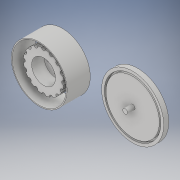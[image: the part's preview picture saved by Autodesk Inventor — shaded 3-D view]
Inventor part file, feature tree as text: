
AUTODESK INVENTOR PART (.ipt)
format: ipt  version: 2017 SP1 (Build 210196100, 196)  size: 249,344 bytes
history: native  units: in
note: dims shown in document units (in); Inventor stores cm internally (conversion verified against a paired STEP export)
features: extrude x7, sketch x7
ambient origin geometry x8: Origin, YZ Plane, XZ Plane, XY Plane, X Axis, Y Axis, Z Axis, Center Point
bodies: Solid1 (feature_tree)
feature tree (14):
  extrude  "Hub Mount"  Depth=0.1122in
  extrude  "Tire Mount"  Depth=0.1122in
  extrude  "Tire Grip Extrusion"  Depth=0.1575in
  extrude  "Tire Mold Shell"  Depth=0.25in
  extrude  "Tire Mold Base"  Depth=0.25in
  extrude  "Inset into base for shell"  Depth=0.1969in
  extrude  "Extrusion7"  Depth=0.5906in TaperAngle=0.0deg
  sketch  "Sketch1"  dims[d0=0.748in d1=0.1122in]
  sketch  "Sketch2"  dims[d2=0.1122in d3=0.1122in]
  sketch  "Sketch4"  dims[d4=0.1122in d5=0.1575in]
  sketch  "Sketch5"  dims[d6=0.25in d7=0.25in]
  sketch  "Sketch6"  dims[d8=0.25in d9=0.25in]
  sketch  "Sketch7"  dims[d10=0.1969in d11=0.0in d12=0.748in]
  sketch  "Sketch8"  dims[d13=1.2598in d14=0.5906in d15=0.0in d21=0.1181in d22=0.1181in d23=0.1181in d24=0.1181in d29=0.1181in d30=22.5deg d31=22.5deg d32=22.5deg d33=22.5deg d34=22.5deg d35=22.5deg d36=22.5deg d37=22.5deg d38=22.5deg d39=22.5deg d40=22.5deg d41=22.5deg d42=0.1181in d43=0.1181in d44=0.1181in d45=0.1181in d46=0.1181in d47=0.1181in d48=0.1181in d49=0.1181in d50=0.1181in d51=0.1181in d52=0.1181in d53=0.5906in d54=0.0in d55=1.6929in d56=1.752in d57=0.7283in d58=0.0in d59=1.9488in d60=2.3622in d63=0.1575in d64=0.0in d65=1.6732in d66=1.7717in d67=2.3622in d68=0.0984in d69=0.0in d70=0.1496in d71=2.3622in d72=0.2362in d73=0.0in]
